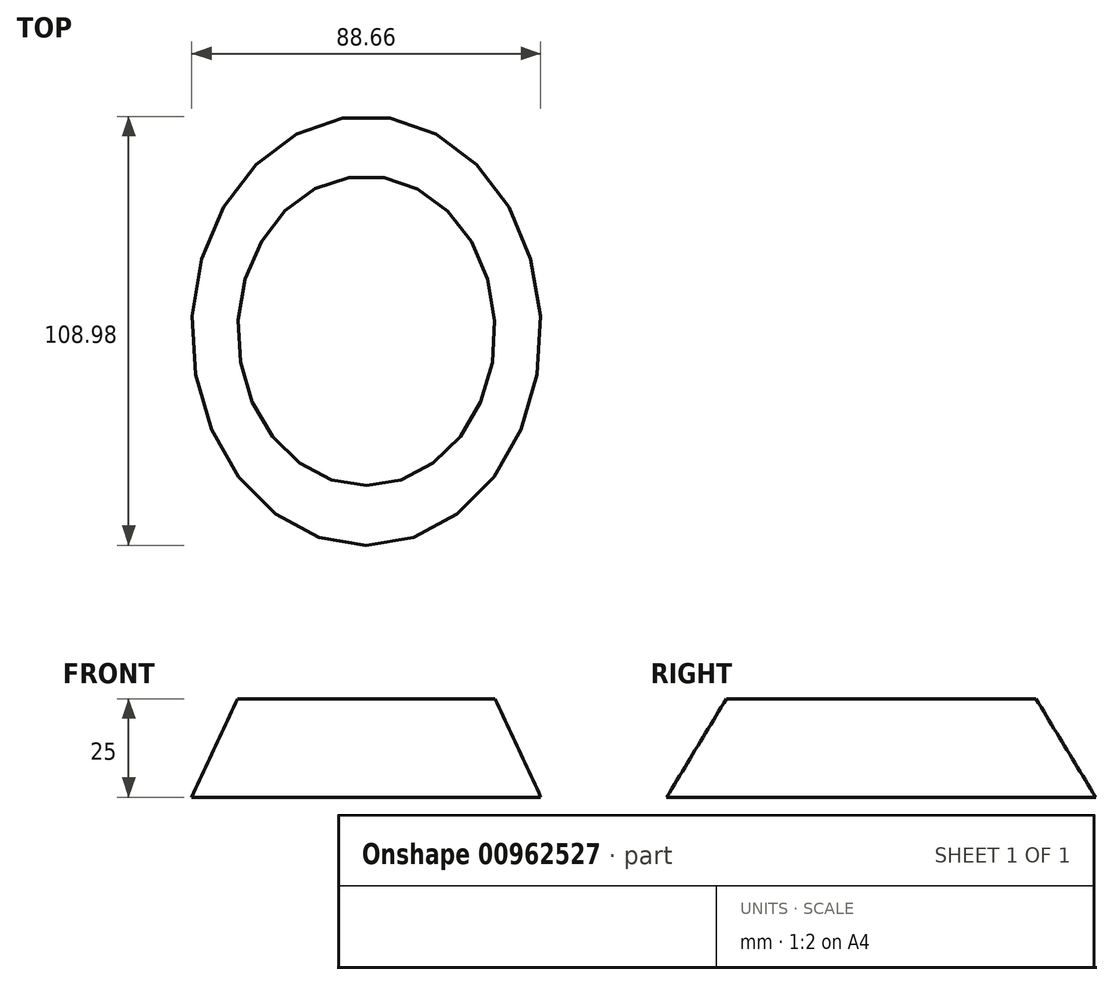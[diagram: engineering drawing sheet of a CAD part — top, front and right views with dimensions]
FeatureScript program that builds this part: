
annotation { "Feature Type Name" : "Feature", "Feature Type Description" : "" }
export const myFeature = defineFeature(function(context is Context, id is Id, definition is map)
    precondition{}
    {
        {
            var Q0;
            Q0=qCreatedBy(makeId("Top.planeOp"),FACE);
            var sketch = newSketch(context, id + "F0", { "sketchPlane" : qUnion([Q0])});
            skEllipse(sketch, "E0", {"center": v(-2.2, -1.2) * mm, "majorRadius": 54.5 * mm, "minorRadius": 44.33 * mm, "majorAxis": v(0, -1)});
            skEllipse(sketch, "E1", {"center": v(-2.2, -1.2) * mm, "majorRadius": 59.1 * mm, "minorRadius": 48.05 * mm, "majorAxis": v(0.03, -1)});
            skSolve(sketch);
        }
        {
            var Q0;
            Q0=qCreatedBy(makeId("Top.planeOp"),FACE);
            cPlane(context, id + "F1", {"entities" : qUnion([Q0]), "cplaneType" : CPlaneType.OFFSET, "offset" : 25 * mm, "width" : 150 * mm, "height" : 150 * mm});
        }
        {
            var Q0;
            Q0=qCreatedBy(id+"F1.planeOp",FACE);
            var sketch = newSketch(context, id + "F2", { "sketchPlane" : qUnion([Q0])});
            skEllipse(sketch, "E2", {"center": v(-2.16, -1.2) * mm, "majorRadius": 39.34 * mm, "minorRadius": 32.68 * mm, "majorAxis": v(0, -1)});
            skEllipse(sketch, "E3", {"center": v(-2.16, -1.2) * mm, "majorRadius": 42.72 * mm, "minorRadius": 36.57 * mm, "majorAxis": v(0, -1)});
            skSolve(sketch);
        }
        {
            var Q0;
            Q0=makeQuery(id+"F0.imprint","IMPRINT",FACE,{"disambiguationData":[TD([[makeQuery(id+"F0.imprint","IMPRINT",EDGE,{"derivedFrom":sQuery(id+"F0.wireOp",EDGE,"E0")}),1.0]])]});
            var Q1;
            Q1=makeQuery(id+"F2.imprint","IMPRINT",FACE,{"disambiguationData":[TD([[makeQuery(id+"F2.imprint","IMPRINT",EDGE,{"derivedFrom":sQuery(id+"F2.wireOp",EDGE,"E2")}),1.0]])]});
            loft(context, id + "F3", {"sheetProfilesArray" : [{ "sheetProfileEntities" : qUnion([Q0]) }, { "sheetProfileEntities" : qUnion([Q1]) }]});
        }
    });
